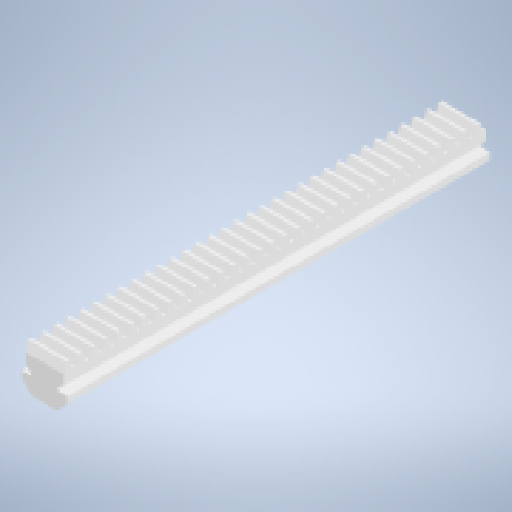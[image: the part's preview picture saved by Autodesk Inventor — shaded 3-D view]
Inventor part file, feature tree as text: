
AUTODESK INVENTOR PART (.ipt)
format: ipt  version: 2023.2 (Build 272271000, 271)  size: 842,752 bytes
history: native  units: mm
features: extrude x2, sketch x2, projected_geometry x1
ambient origin geometry x8: Origin, YZ Plane, XZ Plane, XY Plane, X Axis, Y Axis, Z Axis, Center Point
bodies: Body1 (feature_tree)
feature tree (5):
  extrude  "Extrusion3"  Depth=0.15mm
  extrude  "Extrusion7"  Depth=98.27mm TaperAngle=0.0deg
  sketch  "Sketch1"  dims[d9=0.15mm d10=0.15mm]
  sketch  "Sketch7"  dims[d11=0.15mm d12=98.27mm d13=0.0mm d68=4.4mm d69=2.3mm d70=0.672mm d71=12.217305mm d72=12.217305mm d73=2.978358mm d74=330.0mm d76=2.978mm d77=10.0mm d79=10.0mm d81=98.27mm d82=0.0mm d61=1.0mm d62=1.0mm d63=1.0mm d64=0.15mm d65=0.25mm d66=0.375mm d67=14.3117mm]
  projected_geometry  "Projected Loop2"
